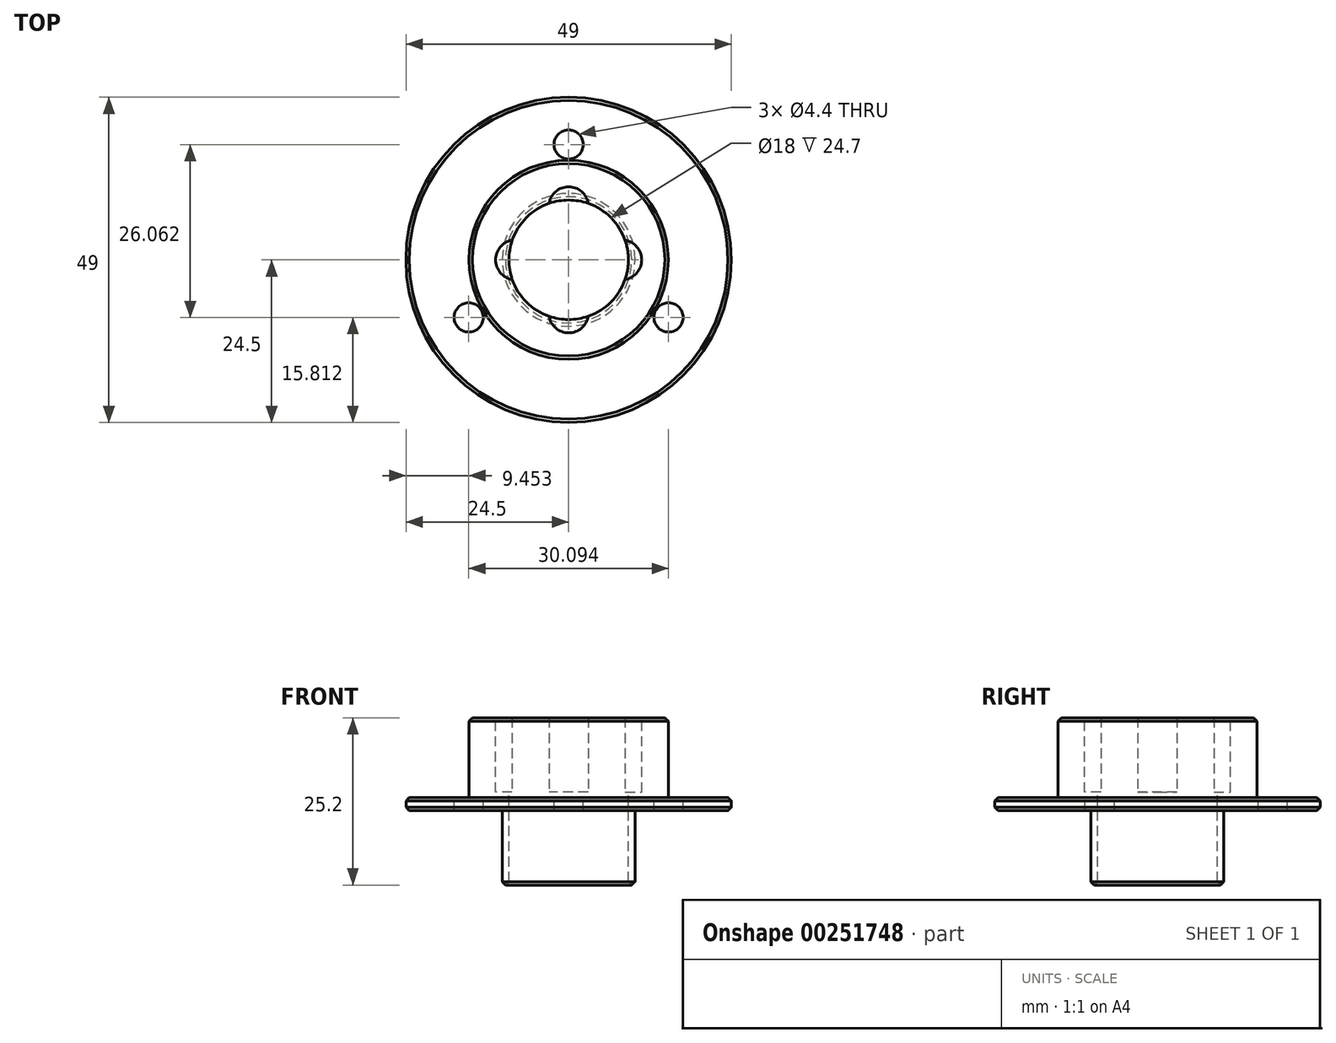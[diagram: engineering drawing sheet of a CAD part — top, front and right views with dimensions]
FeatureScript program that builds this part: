
annotation { "Feature Type Name" : "Feature", "Feature Type Description" : "" }
export const myFeature = defineFeature(function(context is Context, id is Id, definition is map)
    precondition{}
    {
        {
            var Q0;
            Q0=qCreatedBy(makeId("Top.planeOp"),FACE);
            var sketch = newSketch(context, id + "F0", { "sketchPlane" : qUnion([Q0])});
            skCircle(sketch, "E0", {"center": v(0, 0) * mm, "radius": 24.5 * mm});
            skCircle(sketch, "E1", {"center": v(0, 0) * mm, "radius": 15 * mm});
            skSolve(sketch);
        }
        {
            var Q0;
            Q0 = qSketchRegion(id + "F0", true);
            extrude(context, id + "F1", {"entities" : qUnion([Q0]), "depth" : 2 * mm});
        }
        {
            var Q0;
            Q0=qCreatedBy(makeId("Top.planeOp"),FACE);
            var sketch = newSketch(context, id + "F2", { "sketchPlane" : qUnion([Q0])});
            skCircle(sketch, "E2.0", {"center": v(0, 0) * mm, "radius": 15 * mm});
            skSolve(sketch);
        }
        {
            var Q0;
            Q0 = qSketchRegion(id + "F2", true);
            extrude(context, id + "F3", {"entities" : qUnion([Q0]), "operationType" : NewBodyOperationType.ADD, "depth" : 14 * mm});
        }
        {
            var Q0;
            Q0=makeQuery(id+"F3.opExtrude","CAP_FACE",FACE,{"disambiguationData":[OSD([sQuery(id+"F2.wireOp",EDGE,"E2.0")])],"isStart":false});
            var sketch = newSketch(context, id + "F4", { "sketchPlane" : qUnion([Q0])});
            skCircle(sketch, "E3", {"center": v(0, 0) * mm, "radius": 8 * mm});
            skArc(sketch, "E4", {"start": v(2.95, 7.44) * mm, "mid": v(0, 11) * mm, "end": v(-2.95, 7.44) * mm});
            skArc(sketch, "E5", {"start": v(7.44, -2.95) * mm, "mid": v(11, 0) * mm, "end": v(7.44, 2.95) * mm});
            skArc(sketch, "E6", {"start": v(-2.95, -7.44) * mm, "mid": v(0, -11) * mm, "end": v(2.95, -7.44) * mm});
            skArc(sketch, "E7", {"start": v(-7.44, 2.95) * mm, "mid": v(-11, 0) * mm, "end": v(-7.44, -2.95) * mm});
            skSolve(sketch);
        }
        {
            var Q0;
            Q0 = qSketchRegion(id + "F4", true);
            extrude(context, id + "F5", {"entities" : qUnion([Q0]), "operationType" : NewBodyOperationType.REMOVE, "oppositeDirection" : true, "depth" : 11.2 * mm});
        }
        {
            var Q0;
            Q0=makeQuery(id+"F5.boolean.opBoolean","COPY",FACE,{"derivedFrom":makeQuery(id+"F5.opExtrude","CAP_FACE",FACE,{"disambiguationData":[OSD([sQuery(id+"F4.wireOp",EDGE,"E3"),sQuery(id+"F4.wireOp",EDGE,"E4"),sQuery(id+"F4.wireOp",EDGE,"E5"),sQuery(id+"F4.wireOp",EDGE,"E6"),sQuery(id+"F4.wireOp",EDGE,"E7")])],"isStart":false})});
            var sketch = newSketch(context, id + "F6", { "sketchPlane" : qUnion([Q0])});
            skCircle(sketch, "E8", {"center": v(0, 0) * mm, "radius": 10 * mm});
            skCircle(sketch, "E9", {"center": v(0, 0) * mm, "radius": 9 * mm});
            skSolve(sketch);
        }
        {
            var Q0;
            Q0 = qSketchRegion(id + "F6", true);
            extrude(context, id + "F7", {"entities" : qUnion([Q0]), "operationType" : NewBodyOperationType.ADD, "oppositeDirection" : true, "depth" : 14 * mm});
        }
        {
            var Q0;
            Q0=makeQuery(id+"F7.boolean.opBoolean","SPLIT",FACE,{"disambiguationData":[TD([makeQuery(id+"F7.opExtrude","SWEPT_FACE",FACE,{"disambiguationData":[OSD([sQuery(id+"F6.wireOp",EDGE,"E9")])]})])],"derivedFrom":makeQuery(id+"F3.boolean.opBoolean","MERGE",FACE,{"derivedFrom":[makeQuery(id+"F1.opExtrude","CAP_FACE",FACE,{"disambiguationData":[OSD([sQuery(id+"F0.wireOp",EDGE,"E0"),sQuery(id+"F0.wireOp",EDGE,"E1")])],"isStart":true}),makeQuery(id+"F3.opExtrude","CAP_FACE",FACE,{"disambiguationData":[OSD([sQuery(id+"F2.wireOp",EDGE,"E2.0")])],"isStart":true})]})});
            extrude(context, id + "F8", {"entities" : qUnion([Q0]), "operationType" : NewBodyOperationType.REMOVE, "oppositeDirection" : true, "depth" : 25 * mm});
        }
        {
            var Q0;
            Q0=makeQuery(id+"F1.opExtrude","CAP_FACE",FACE,{"disambiguationData":[OSD([sQuery(id+"F0.wireOp",EDGE,"E0"),sQuery(id+"F0.wireOp",EDGE,"E1")])],"isStart":false});
            var sketch = newSketch(context, id + "F9", { "sketchPlane" : qUnion([Q0])});
            skPoint(sketch, "E10", {"position": v(0, 17.38) * mm});
            skPoint(sketch, "E11", {"position": v(-15.05, -8.69) * mm});
            skPoint(sketch, "E12", {"position": v(15.05, -8.69) * mm});
            skLineSegment(sketch, "E13", {"start": v(0, 29.8) * mm, "end": v(0, 0) * mm, "construction": true});
            skLineSegment(sketch, "E14", {"start": v(-30.8, -17.78) * mm, "end": v(0, 0) * mm, "construction": true});
            skLineSegment(sketch, "E15", {"start": v(0, 0) * mm, "end": v(29.63, -17.1) * mm, "construction": true});
            skCircle(sketch, "E16", {"center": v(0, 0) * mm, "radius": 17.38 * mm});
            skSolve(sketch);
        }
        {
            var Q0;
            Q0=sQuery(id+"F9.wireOp",VERTEX,"E10");
            var Q1;
            Q1=sQuery(id+"F9.wireOp",VERTEX,"E11");
            var Q2;
            Q2=sQuery(id+"F9.wireOp",VERTEX,"E12");
            var Q3;
            Q3=makeQuery(id+"F1.opExtrude","SWEPT_BODY",BODY,{"disambiguationData":[OSD([sQuery(id+"F0.wireOp",EDGE,"E0"),sQuery(id+"F0.wireOp",EDGE,"E1")])]});
            hole(context, id + "F10", {"style" : HoleStyle.SIMPLE, "endStyle" : HoleEndStyle.THROUGH, "standardTappedOrClearance" : lookupTablePath({ "standard" : "ISO", "fit" : "Normal", "size" : "M4", "type" : "Clearance" }), "standardBlindInLast" : lookupTablePath({ "fit" : "Standard", "standard" : "ISO", "size" : "M4", "type" : "Clearance" }), "holeDiameter" : 4.4 * mm, "isTappedThrough" : true, "tappedDepth" : 12 * mm, "tapClearance" : 3, "locations" : qUnion([Q0, Q1, Q2]), "scope" : qUnion([Q3])});
        }
        {
            var Q0;
            Q0=makeQuery(id+"F3.opExtrude","CAP_EDGE",EDGE,{"disambiguationData":[OSD([sQuery(id+"F2.wireOp",EDGE,"E2.0")])],"isStart":false});
            var Q1;
            Q1=makeQuery(id+"F1.opExtrude","CAP_EDGE",EDGE,{"disambiguationData":[OSD([sQuery(id+"F0.wireOp",EDGE,"E0")])],"isStart":false});
            var Q2;
            Q2=makeQuery(id+"F1.opExtrude","CAP_EDGE",EDGE,{"disambiguationData":[OSD([sQuery(id+"F0.wireOp",EDGE,"E0")])],"isStart":true});
            var Q3;
            Q3=makeQuery(id+"F5.boolean.opBoolean","COPY",EDGE,{"derivedFrom":makeQuery(id+"F5.opExtrude","CAP_EDGE",EDGE,{"disambiguationData":[OSD([sQuery(id+"F4.wireOp",EDGE,"E4")])],"isStart":true})});
            var Q4;
            Q4=makeQuery(id+"F5.boolean.opBoolean","COPY",EDGE,{"derivedFrom":makeQuery(id+"F5.opExtrude","CAP_EDGE",EDGE,{"disambiguationData":[OSD([sQuery(id+"F4.wireOp",EDGE,"E5")])],"isStart":true})});
            var Q5;
            Q5=makeQuery(id+"F5.boolean.opBoolean","COPY",EDGE,{"derivedFrom":makeQuery(id+"F5.opExtrude","CAP_EDGE",EDGE,{"disambiguationData":[OSD([sQuery(id+"F4.wireOp",EDGE,"E6")])],"isStart":true})});
            var Q6;
            Q6=makeQuery(id+"F5.boolean.opBoolean","COPY",EDGE,{"derivedFrom":makeQuery(id+"F5.opExtrude","CAP_EDGE",EDGE,{"disambiguationData":[OSD([sQuery(id+"F4.wireOp",EDGE,"E7")])],"isStart":true})});
            var Q7;
            Q7=makeQuery(id+"F7.opExtrude","CAP_EDGE",EDGE,{"disambiguationData":[OSD([sQuery(id+"F6.wireOp",EDGE,"E8")])],"isStart":false});
            var Q8;
            Q8=makeQuery(id+"F7.opExtrude","CAP_EDGE",EDGE,{"disambiguationData":[OSD([sQuery(id+"F6.wireOp",EDGE,"E9")])],"isStart":false});
            chamfer(context, id + "F11", {"entities" : qUnion([Q0, Q1, Q2, Q3, Q4, Q5, Q6, Q7, Q8]), "chamferType" : ChamferType.OFFSET_ANGLE, "width" : .5 * mm, "oppositeDirection" : false, "angle" : 45 * degree, "tangentPropagation" : true});
        }
    });
